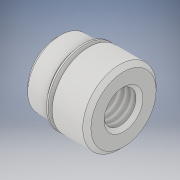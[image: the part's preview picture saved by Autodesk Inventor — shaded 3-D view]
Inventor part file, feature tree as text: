
AUTODESK INVENTOR PART (.ipt)
format: ipt  version: 2018 (Build 220112000, 112)  size: 221,696 bytes
history: native  units: in
note: dims shown in document units (in); Inventor stores cm internally (conversion verified against a paired STEP export)
features: other x84, revolve x3, sketch x3, thread x1
ambient origin geometry x8: Origin, YZ Plane, XZ Plane, XY Plane, X Axis, Y Axis, Z Axis, Center Point
bodies: Solid1 (feature_tree)
feature tree (91):
  revolve  "Revolution1"  Angle=360.0deg
  revolve  "Revolution2"  Angle=360.0deg
  thread  "Thread1"  [1 undecoded]
  revolve  "Revolution3"  [1 undecoded]
  other  "lovra_XY"
  other  "lovra_YZ"
  other  "lovra_ZX"
  other  "lovra_X"
  other  "lovra_Y"
  other  "lovra_Z"
  other  "lovra_Center"
  other  "lovra1_XY"
  other  "lovra1_YZ"
  other  "lovra1_ZX"
  other  "lovra1_X"
  other  "lovra1_Y"
  other  "lovra1_Z"
  other  "lovra1_Center"
  other  "lovra2_XY"
  other  "lovra2_YZ"
  other  "lovra2_ZX"
  other  "lovra2_X"
  other  "lovra2_Y"
  other  "lovra2_Z"
  other  "lovra2_Center"
  other  "lovra21_XY"
  other  "lovra21_YZ"
  other  "lovra21_ZX"
  other  "lovra21_X"
  other  "lovra21_Y"
  other  "lovra21_Z"
  other  "lovra21_Center"
  other  "lovra22_XY"
  other  "lovra22_YZ"
  other  "lovra22_ZX"
  other  "lovra22_X"
  other  "lovra22_Y"
  other  "lovra22_Z"
  other  "lovra22_Center"
  other  "lovra3_XY"
  other  "lovra3_YZ"
  other  "lovra3_ZX"
  other  "lovra3_X"
  other  "lovra3_Y"
  other  "lovra3_Z"
  other  "lovra3_Center"
  other  "olen_XY"
  other  "olen_YZ"
  other  "olen_ZX"
  other  "olen_X"
  other  "olen_Y"
  other  "olen_Z"
  other  "olen_Center"
  other  "to_mounting_bracket_XY"
  other  "to_mounting_bracket_YZ"
  other  "to_mounting_bracket_ZX"
  other  "to_mounting_bracket_X"
  other  "to_mounting_bracket_Y"
  other  "to_mounting_bracket_Z"
  other  "to_mounting_bracket_Center"
  other  "to_nut_XY"
  other  "to_nut_YZ"
  other  "to_nut_ZX"
  other  "to_nut_X"
  other  "to_nut_Y"
  other  "to_nut_Z"
  other  "to_nut_Center"
  other  "to_pin_XY"
  other  "to_pin_YZ"
  other  "to_pin_ZX"
  other  "to_pin_X"
  other  "to_pin_Y"
  other  "to_pin_Z"
  other  "to_pin_Center"
  other  "to_screw_XY"
  other  "to_screw_YZ"
  other  "to_screw_ZX"
  other  "to_screw_X"
  other  "to_screw_Y"
  other  "to_screw_Z"
  other  "to_screw_Center"
  other  "to_tube_XY"
  other  "to_tube_YZ"
  other  "to_tube_ZX"
  other  "to_tube_X"
  other  "to_tube_Y"
  other  "to_tube_Z"
  other  "to_tube_Center"
  sketch  "Sketch_1"  dims[d0=360.0deg d1=360.0deg]
  sketch  "Sketch_2"  dims[d2=0.2942in d3=0.0in d4=360.0deg]
  sketch  "Sketch_24"  dims[d5=0.0in d6=0.0in d7=0.0in d8=0.0in d9=0.0in d10=0.0in]
note: 2 required parameter values undecoded (feature->parameter linkage not recoverable at this tier; creation-order binding heuristic only, values carry confidence <= 0.55)
